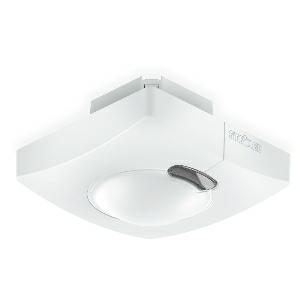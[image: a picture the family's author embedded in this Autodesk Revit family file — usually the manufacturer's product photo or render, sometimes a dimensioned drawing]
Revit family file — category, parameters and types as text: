
# Revit family: hf_3360_033705
name_source: partatom
category: Elektroinstallationen
revit_build: Autodesk Revit 2016 (Build: 20190508_0715(x64)
units: mm (PartAtom-declared; Revit-internal decimal feet)

## family parameters
Basisbauteil = Fläche
Beim Laden mit Abzugskörper schneiden = Nein
Bemaßung runder Anschluss = Durchmesser verwenden
Beschriftungsausrichtung beibehalten = Nein
Gemeinsam genutzt = Nein
Raumberechnungspunkt = Nein
Teiletyp = Normal

## types (1)
- HF 3360
    Apparent Load = 0 VA
    Beschreibung = Type: Motion detectors; Dimensions (L x W x H): 64 x 94 x 94 mm; Mains power supply: 220 – 240 V / 50 – 60 Hz; Sensor Technology: High frequency; Application, place: Indoors; Application, room: function room / ancillary room, stairwell, WC / washroom, multi-storey / underground car park, Indoors; Installation site: wall, ceiling, corner; Installation: Concealed wiring; HF-system: 5,8 GHz; Electronic scalability: Yes; Mechanical scalability: No; Mounting height: 2,00 – 4,00 m; Optimum mounting height: 2,8 m; Detection: also through glass, wood and stud walls; Detection angle: 360 °; Angle of aperture: 140 °; Sneak-by guard: Yes; Reach, radial: Ø 8 m (50 m²); Reach, tangential: Ø 8 m (50 m²); Twilight setting TEACH: Yes; Twilight setting: 2 – 1000 lx; Time setting: 5 sec – 15 min; Constant-lighting control: No; Basic light level function: No; Functions: Normal / test mode, Manual ON / ON-OFF; Settings via: Remote control, Potentiometers, Smart Remote; With remote control: No; Interconnection: Yes; IP-rating: IP20; Material: Plastic; Ambient temperature: -20 – 50 °C; Colour: white; Colour, RAL: 9003; Manufacturer's Warranty: 5 years; Version: PF - concealed, sq.; PU1, EAN: 4007841033705
    Height = 94 mm  [stored 0.308399 ft]
    Hersteller = Steinel
    Length = 64 mm
    ModVariant = Nein
    Modell = 033705
    Mounting Type = Recessed
    Number of Poles = 1
    OnlyDefault = Ja
    Power Factor = 1
    Product Name = HF 3360
    Product group = Sensor-switched indoor light
    ProductGroupID = 30
    Protection Class = Protection class
    Protection Degree = IP 20
    RlxData = <blob elided: 26737 chars, md5=084d0b4d>
    SensorDataFile = {"IESDataFiles":[]}
    Typenbild = produkt1_033705.jpg
    Typenkommentare = Product without accessories
    URL = http://relux.com
    VarID = ---
    Voltage = 0 V
    Vorgabe-Ansicht = 1800 mm
    Weight = 0.00 kg
    Width = 94 mm  [stored 0.308399 ft]

note: [stored X ft] marks values corroborated as IEEE doubles in the binary element streams (Revit-internal decimal feet)

## geometry (parser evidence)
native form markers: Blend x4, Sweep x12
no freeform markers — native parametric forms only
